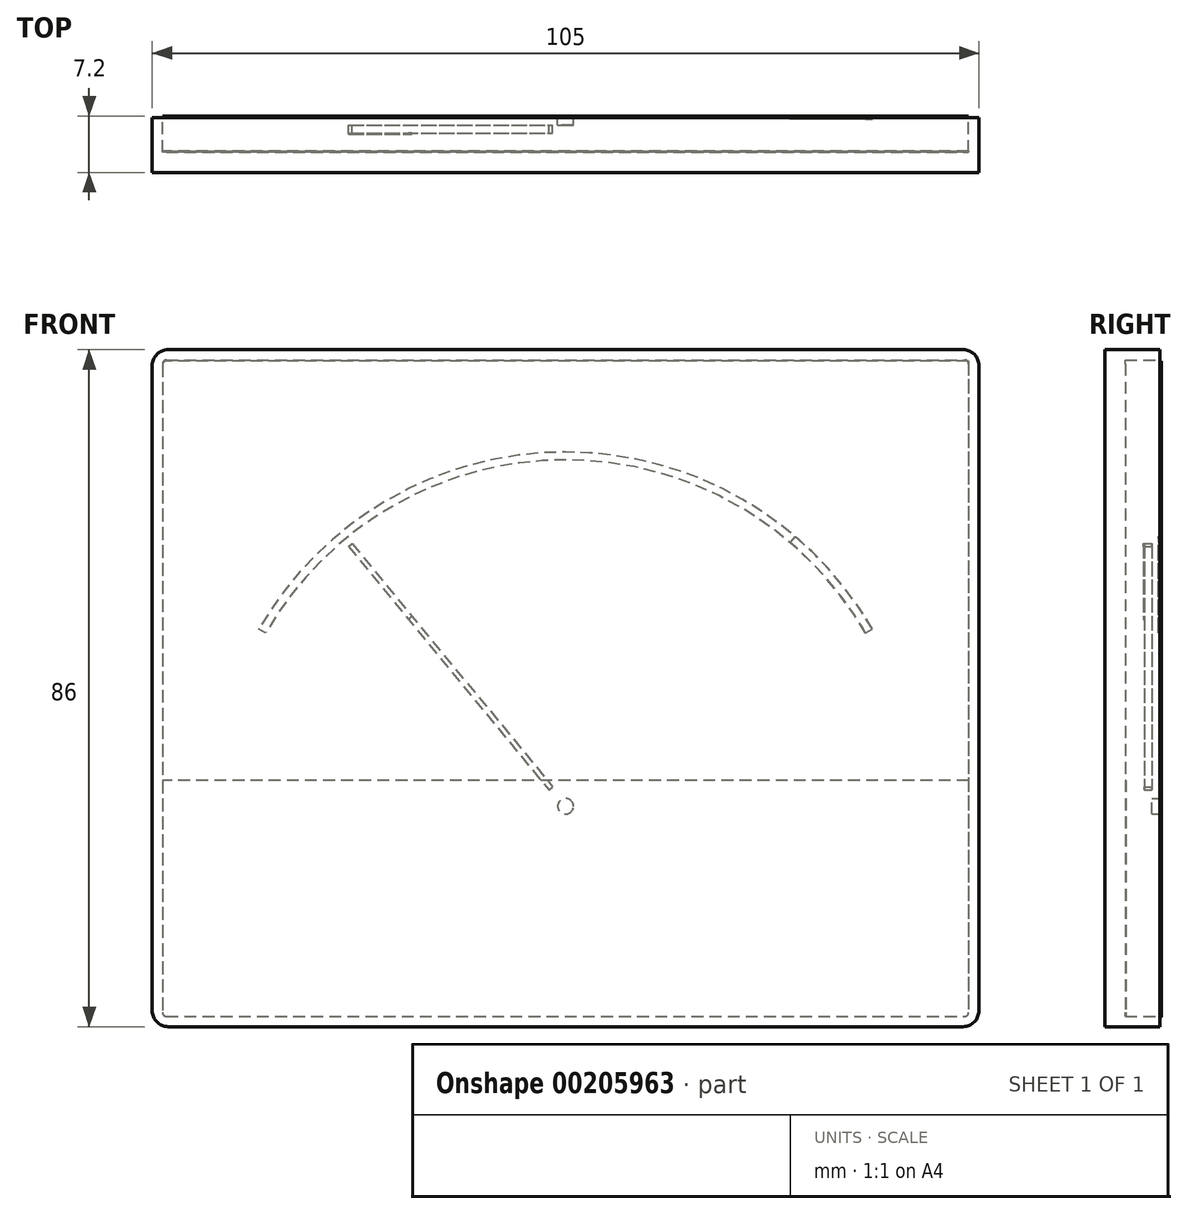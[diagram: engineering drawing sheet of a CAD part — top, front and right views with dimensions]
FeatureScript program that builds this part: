
annotation { "Feature Type Name" : "Feature", "Feature Type Description" : "" }
export const myFeature = defineFeature(function(context is Context, id is Id, definition is map)
    precondition{}
    {
        {
            var Q0;
            Q0=qCreatedBy(makeId("Front.planeOp"),FACE);
            var sketch = newSketch(context, id + "F0", { "sketchPlane" : qUnion([Q0])});
            skLineSegment(sketch, "E0.bottom", {"start": v(-50.5, 43) * mm, "end": v(50.5, 43) * mm});
            skLineSegment(sketch, "E0.top", {"start": v(-50.5, -43) * mm, "end": v(50.5, -43) * mm});
            skLineSegment(sketch, "E0.left", {"start": v(-52.5, 41) * mm, "end": v(-52.5, -41) * mm});
            skLineSegment(sketch, "E0.right", {"start": v(52.5, 41) * mm, "end": v(52.5, -41) * mm});
            skLineSegment(sketch, "E1", {"start": v(0, 0) * mm, "end": v(52.5, 0) * mm, "construction": true});
            skLineSegment(sketch, "E2", {"start": v(0, 0) * mm, "end": v(0, 43) * mm, "construction": true});
            skPoint(sketch, "E3.visualSharp", {"position": v(52.5, 43) * mm});
            skArc(sketch, "E3.filletArc", {"start": v(52.5, 41) * mm, "mid": v(51.91, 42.41) * mm, "end": v(50.5, 43) * mm});
            skPoint(sketch, "E4.visualSharp", {"position": v(-52.5, 43) * mm});
            skArc(sketch, "E4.filletArc", {"start": v(-50.5, 43) * mm, "mid": v(-51.91, 42.41) * mm, "end": v(-52.5, 41) * mm});
            skPoint(sketch, "E5.visualSharp", {"position": v(-52.5, -43) * mm});
            skArc(sketch, "E5.filletArc", {"start": v(-52.5, -41) * mm, "mid": v(-51.91, -42.41) * mm, "end": v(-50.5, -43) * mm});
            skPoint(sketch, "E6.visualSharp", {"position": v(52.5, -43) * mm});
            skArc(sketch, "E6.filletArc", {"start": v(50.5, -43) * mm, "mid": v(51.91, -42.41) * mm, "end": v(52.5, -41) * mm});
            skSolve(sketch);
        }
        {
            var Q0;
            Q0 = qSketchRegion(id + "F0", true);
            extrude(context, id + "F1", {"entities" : qUnion([Q0]), "depth" : 7 * mm});
        }
        {
            var Q0;
            Q0=makeQuery(id+"F1.opExtrude","CAP_FACE",FACE,{"disambiguationData":[OSD([sQuery(id+"F0.wireOp",EDGE,"E0.bottom"),sQuery(id+"F0.wireOp",EDGE,"E0.top"),sQuery(id+"F0.wireOp",EDGE,"E0.left"),sQuery(id+"F0.wireOp",EDGE,"E0.right")])],"isStart":true});
            var sketch = newSketch(context, id + "F2", { "sketchPlane" : qUnion([Q0])});
            skLineSegment(sketch, "E7.0", {"start": v(50.7, -41.7) * mm, "end": v(-50.7, -41.7) * mm});
            skLineSegment(sketch, "E7.1", {"start": v(51.2, 41.2) * mm, "end": v(51.2, -41.2) * mm});
            skLineSegment(sketch, "E7.2", {"start": v(50.7, 41.7) * mm, "end": v(-50.7, 41.7) * mm});
            skLineSegment(sketch, "E7.3", {"start": v(-51.2, 41.2) * mm, "end": v(-51.2, -41.2) * mm});
            skPoint(sketch, "E8.visualSharp", {"position": v(-51.2, -41.7) * mm});
            skArc(sketch, "E8.filletArc", {"start": v(-51.2, -41.2) * mm, "mid": v(-51.05, -41.55) * mm, "end": v(-50.7, -41.7) * mm});
            skPoint(sketch, "E9.visualSharp", {"position": v(51.2, -41.7) * mm});
            skArc(sketch, "E9.filletArc", {"start": v(50.7, -41.7) * mm, "mid": v(51.05, -41.55) * mm, "end": v(51.2, -41.2) * mm});
            skPoint(sketch, "E10.visualSharp", {"position": v(51.2, 41.7) * mm});
            skArc(sketch, "E10.filletArc", {"start": v(51.2, 41.2) * mm, "mid": v(51.05, 41.55) * mm, "end": v(50.7, 41.7) * mm});
            skPoint(sketch, "E11.visualSharp", {"position": v(-51.2, 41.7) * mm});
            skArc(sketch, "E11.filletArc", {"start": v(-50.7, 41.7) * mm, "mid": v(-51.05, 41.55) * mm, "end": v(-51.2, 41.2) * mm});
            skSolve(sketch);
        }
        {
            var Q0;
            Q0 = qSketchRegion(id + "F2", true);
            var Q1;
            Q1=makeQuery(id+"F1.opExtrude","CAP_FACE",FACE,{"disambiguationData":[OSD([sQuery(id+"F0.wireOp",EDGE,"E0.bottom"),sQuery(id+"F0.wireOp",EDGE,"E0.top"),sQuery(id+"F0.wireOp",EDGE,"E0.left"),sQuery(id+"F0.wireOp",EDGE,"E0.right"),sQuery(id+"F0.wireOp",EDGE,"E3.filletArc"),sQuery(id+"F0.wireOp",EDGE,"E4.filletArc"),sQuery(id+"F0.wireOp",EDGE,"E5.filletArc"),sQuery(id+"F0.wireOp",EDGE,"E6.filletArc")])],"isStart":false});
            extrude(context, id + "F3", {"entities" : qUnion([Q0]), "operationType" : NewBodyOperationType.REMOVE, "oppositeDirection" : true, "endBoundEntityFace" : qUnion([Q1]), "depth" : 4.4 * mm});
        }
        {
            var Q0;
            Q0=makeQuery(id+"F1.opExtrude","CAP_FACE",FACE,{"disambiguationData":[OSD([sQuery(id+"F0.wireOp",EDGE,"E0.bottom"),sQuery(id+"F0.wireOp",EDGE,"E0.top"),sQuery(id+"F0.wireOp",EDGE,"E0.left"),sQuery(id+"F0.wireOp",EDGE,"E0.right"),sQuery(id+"F0.wireOp",EDGE,"E3.filletArc"),sQuery(id+"F0.wireOp",EDGE,"E4.filletArc"),sQuery(id+"F0.wireOp",EDGE,"E5.filletArc"),sQuery(id+"F0.wireOp",EDGE,"E6.filletArc")])],"isStart":true});
            var sketch = newSketch(context, id + "F4", { "sketchPlane" : qUnion([Q0])});
            skPoint(sketch, "E12.firstSnap0", {"position": v(-51.05, 41.55) * mm});
            skLineSegment(sketch, "E12.bottom", {"start": v(-51.2, 41.55) * mm, "end": v(50.7, 41.55) * mm});
            skLineSegment(sketch, "E12.top", {"start": v(-50.7, -41.7) * mm, "end": v(50.7, -41.7) * mm});
            skLineSegment(sketch, "E12.left", {"start": v(-51.2, 41.55) * mm, "end": v(-51.2, -41.2) * mm});
            skLineSegment(sketch, "E12.right", {"start": v(51.2, 41.05) * mm, "end": v(51.2, -41.2) * mm});
            skPoint(sketch, "E13.visualSharp", {"position": v(-51.2, -41.7) * mm});
            skArc(sketch, "E13.filletArc", {"start": v(-51.2, -41.2) * mm, "mid": v(-51.05, -41.55) * mm, "end": v(-50.7, -41.7) * mm});
            skPoint(sketch, "E14.visualSharp", {"position": v(51.2, 41.55) * mm});
            skArc(sketch, "E14.filletArc", {"start": v(51.2, 41.05) * mm, "mid": v(51.05, 41.4) * mm, "end": v(50.7, 41.55) * mm});
            skPoint(sketch, "E15.visualSharp", {"position": v(51.2, -41.7) * mm});
            skArc(sketch, "E15.filletArc", {"start": v(50.7, -41.7) * mm, "mid": v(51.05, -41.55) * mm, "end": v(51.2, -41.2) * mm});
            skSolve(sketch);
        }
        {
            var Q0;
            Q0 = qSketchRegion(id + "F4", true);
            extrude(context, id + "F5", {"entities" : qUnion([Q0]), "depth" : .2 * mm});
        }
        {
            var Q0;
            Q0=makeQuery(id+"F5.opExtrude","CAP_FACE",FACE,{"disambiguationData":[OSD([sQuery(id+"F4.wireOp",EDGE,"E12.bottom"),sQuery(id+"F4.wireOp",EDGE,"E12.top"),sQuery(id+"F4.wireOp",EDGE,"E12.left"),sQuery(id+"F4.wireOp",EDGE,"E12.right"),sQuery(id+"F4.wireOp",EDGE,"E13.filletArc"),sQuery(id+"F4.wireOp",EDGE,"E14.filletArc"),sQuery(id+"F4.wireOp",EDGE,"E15.filletArc")])],"isStart":true});
            var sketch = newSketch(context, id + "F6", { "sketchPlane" : qUnion([Q0])});
            skArc(sketch, "E16", {"start": v(-38.97, 7.5) * mm, "mid": v(0, 30) * mm, "end": v(38.97, 7.5) * mm});
            skArc(sketch, "E17.0", {"start": v(-38.1, 7) * mm, "mid": v(0, 29) * mm, "end": v(38.1, 7) * mm});
            skLineSegment(sketch, "E18", {"start": v(-38.1, 7) * mm, "end": v(-38.97, 7.5) * mm});
            skLineSegment(sketch, "E19", {"start": v(38.1, 7) * mm, "end": v(38.97, 7.5) * mm});
            skLineSegment(sketch, "E20", {"start": v(0, -15) * mm, "end": v(-12.03, -15) * mm, "construction": true});
            skSolve(sketch);
        }
        {
            var Q0;
            Q0 = qSketchRegion(id + "F6", true);
            extrude(context, id + "F7", {"entities" : qUnion([Q0]), "depth" : .1 * mm});
        }
        {
            var Q0;
            Q0=makeQuery(id+"F6.imprint","IMPRINT",FACE,{"disambiguationData":[TD([[makeQuery(id+"F6.imprint","IMPRINT",EDGE,{"derivedFrom":sQuery(id+"F6.wireOp",EDGE,"E16")}),1.0]])]});
            var sketch = newSketch(context, id + "F8", { "sketchPlane" : qUnion([Q0])});
            skCircle(sketch, "E21", {"center": v(0, -15) * mm, "radius": 1 * mm});
            skSolve(sketch);
        }
        {
            var Q0;
            Q0 = qSketchRegion(id + "F8", true);
            extrude(context, id + "F9", {"entities" : qUnion([Q0]), "operationType" : NewBodyOperationType.ADD, "depth" : 1 * mm});
        }
        {
            var Q0;
            Q0=makeQuery(id+"F9.opExtrude","CAP_FACE",FACE,{"disambiguationData":[OSD([sQuery(id+"F8.wireOp",EDGE,"E21")])],"isStart":false});
            var sketch = newSketch(context, id + "F10", { "sketchPlane" : qUnion([Q0])});
            skLineSegment(sketch, "E22", {"start": v(0, -15) * mm, "end": v(-27.34, 18.2) * mm, "construction": true});
            skLineSegment(sketch, "E23", {"start": v(-27.1, 18.38) * mm, "end": v(-1.64, -12.54) * mm});
            skLineSegment(sketch, "E24", {"start": v(-27.57, 18) * mm, "end": v(-2.1, -12.92) * mm});
            skLineSegment(sketch, "E25", {"start": v(-27.57, 18) * mm, "end": v(-27.1, 18.38) * mm});
            skLineSegment(sketch, "E26", {"start": v(-2.1, -12.92) * mm, "end": v(-1.64, -12.54) * mm});
            skSolve(sketch);
        }
        {
            var Q0;
            Q0 = qSketchRegion(id + "F10", true);
            extrude(context, id + "F11", {"entities" : qUnion([Q0]), "depth" : 1 * mm});
        }
        {
            var Q0;
            Q0=makeQuery(id+"F11.opExtrude","CAP_FACE",FACE,{"disambiguationData":[OSD([sQuery(id+"F10.wireOp",EDGE,"E23"),sQuery(id+"F10.wireOp",EDGE,"E24"),sQuery(id+"F10.wireOp",EDGE,"E25"),sQuery(id+"F10.wireOp",EDGE,"E26")])],"isStart":false});
            var sketch = newSketch(context, id + "F12", { "sketchPlane" : qUnion([Q0])});
            skLineSegment(sketch, "E27.0", {"start": v(-27.57, 18) * mm, "end": v(-19.94, 8.74) * mm});
            skLineSegment(sketch, "E28.0", {"start": v(-27.1, 18.38) * mm, "end": v(-19.48, 9.12) * mm});
            skLineSegment(sketch, "E29.0", {"start": v(-27.57, 18) * mm, "end": v(-27.1, 18.38) * mm});
            skLineSegment(sketch, "E30", {"start": v(-19.48, 9.12) * mm, "end": v(-19.94, 8.74) * mm});
            skPoint(sketch, "E31.orphan", {"position": v(-2.1, -12.92) * mm});
            skPoint(sketch, "E32.orphan", {"position": v(-1.64, -12.54) * mm});
            skSolve(sketch);
        }
        {
            var Q0;
            Q0 = qSketchRegion(id + "F12", true);
            extrude(context, id + "F13", {"entities" : qUnion([Q0]), "depth" : .1 * mm});
        }
        {
            var Q0;
            Q0=makeQuery(id+"F3.boolean.opBoolean","COPY",FACE,{"derivedFrom":makeQuery(id+"F3.opExtrude","CAP_FACE",FACE,{"disambiguationData":[OSD([sQuery(id+"F2.wireOp",EDGE,"E7.0"),sQuery(id+"F2.wireOp",EDGE,"E7.1"),sQuery(id+"F2.wireOp",EDGE,"E7.2"),sQuery(id+"F2.wireOp",EDGE,"E7.3"),sQuery(id+"F2.wireOp",EDGE,"E8.filletArc"),sQuery(id+"F2.wireOp",EDGE,"E9.filletArc"),sQuery(id+"F2.wireOp",EDGE,"E10.filletArc"),sQuery(id+"F2.wireOp",EDGE,"E11.filletArc")])],"isStart":false})});
            var sketch = newSketch(context, id + "F14", { "sketchPlane" : qUnion([Q0])});
            skLineSegment(sketch, "E33", {"start": v(-51.2, -11.7) * mm, "end": v(51.2, -11.7) * mm});
            skLineSegment(sketch, "E34.0", {"start": v(-51.2, -11.7) * mm, "end": v(-51.2, -41.2) * mm});
            skArc(sketch, "E35.0", {"start": v(-51.2, -41.2) * mm, "mid": v(-51.05, -41.55) * mm, "end": v(-50.7, -41.7) * mm});
            skLineSegment(sketch, "E35.1", {"start": v(50.7, -41.7) * mm, "end": v(-50.7, -41.7) * mm});
            skArc(sketch, "E35.2", {"start": v(50.7, -41.7) * mm, "mid": v(51.05, -41.55) * mm, "end": v(51.2, -41.2) * mm});
            skLineSegment(sketch, "E35.3", {"start": v(51.2, -11.7) * mm, "end": v(51.2, -41.2) * mm});
            skPoint(sketch, "E36.orphan", {"position": v(-51.2, 41.2) * mm});
            skPoint(sketch, "E37.orphan", {"position": v(51.2, 41.2) * mm});
            skSolve(sketch);
        }
        {
            var Q0;
            Q0 = qSketchRegion(id + "F14", true);
            extrude(context, id + "F15", {"entities" : qUnion([Q0]), "depth" : .1 * mm});
        }
        {
            var Q0;
            Q0=makeQuery(id+"F7.opExtrude","CAP_FACE",FACE,{"disambiguationData":[OSD([sQuery(id+"F6.wireOp",EDGE,"E16"),sQuery(id+"F6.wireOp",EDGE,"E17.0"),sQuery(id+"F6.wireOp",EDGE,"E18"),sQuery(id+"F6.wireOp",EDGE,"E19")])],"isStart":false});
            var sketch = newSketch(context, id + "F16", { "sketchPlane" : qUnion([Q0])});
            skArc(sketch, "E38.0", {"start": v(-38.1, 7) * mm, "mid": v(0, 29) * mm, "end": v(38.1, 7) * mm});
            skArc(sketch, "E38.1", {"start": v(-38.97, 7.5) * mm, "mid": v(0, 30) * mm, "end": v(38.97, 7.5) * mm});
            skLineSegment(sketch, "E38.2", {"start": v(38.1, 7) * mm, "end": v(38.97, 7.5) * mm});
            skLineSegment(sketch, "E39", {"start": v(29.15, 19.28) * mm, "end": v(28.5, 18.52) * mm});
            skSolve(sketch);
        }
        {
            var Q0;
            Q0 = qSketchRegion(id + "F16", true);
            extrude(context, id + "F17", {"entities" : qUnion([Q0]), "depth" : .1 * mm});
        }
    });
